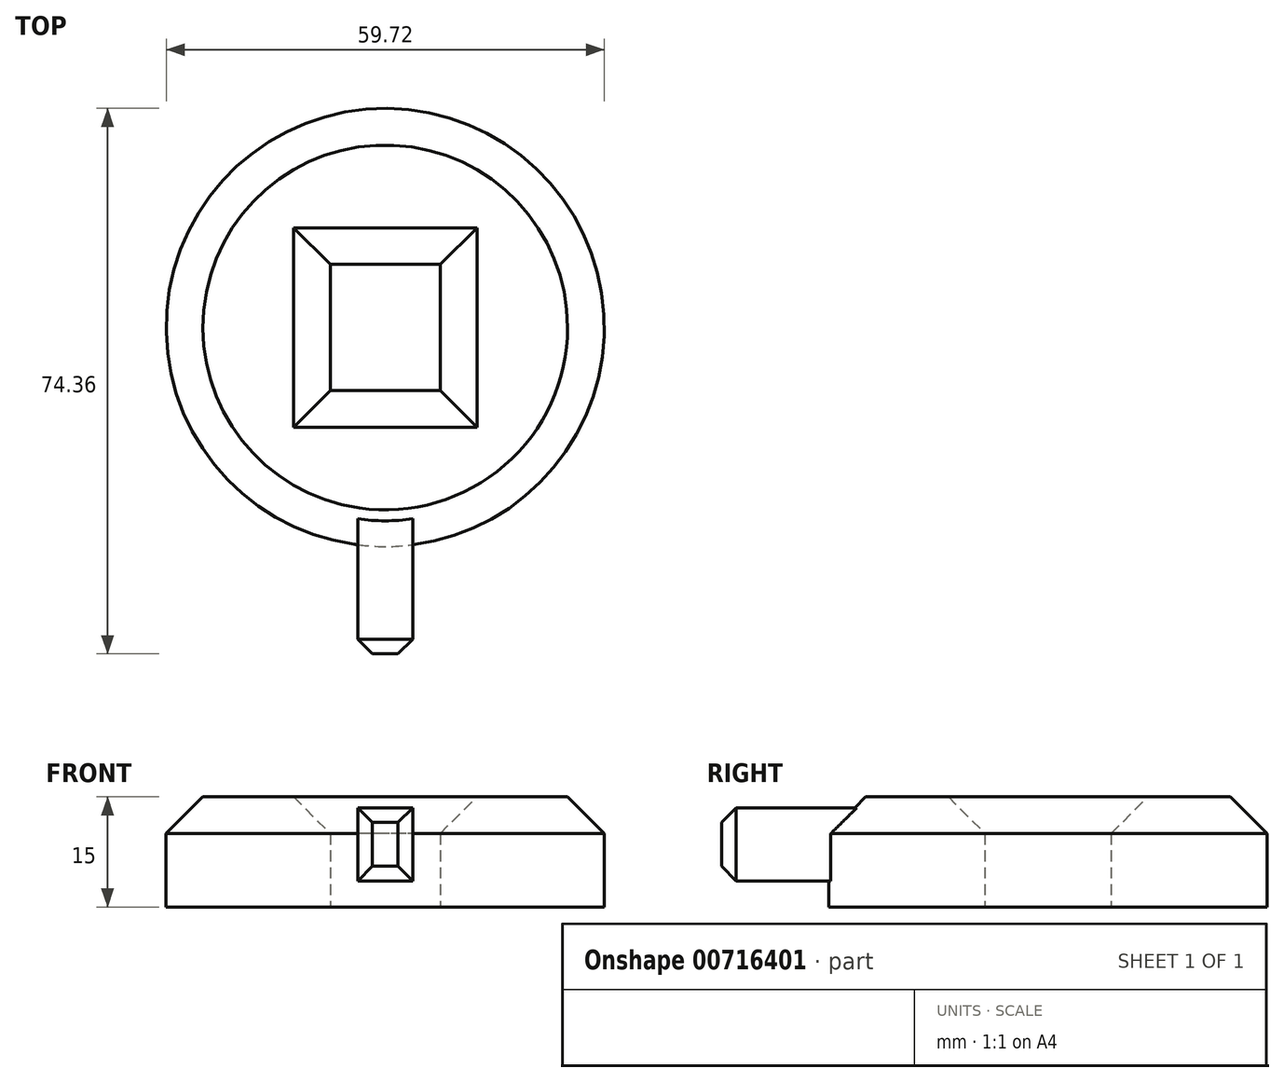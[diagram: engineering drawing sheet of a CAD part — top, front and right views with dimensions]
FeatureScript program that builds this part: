
annotation { "Feature Type Name" : "Feature", "Feature Type Description" : "" }
export const myFeature = defineFeature(function(context is Context, id is Id, definition is map)
    precondition{}
    {
        {
            var Q0;
            Q0=qCreatedBy(makeId("Top.planeOp"),FACE);
            var sketch = newSketch(context, id + "F0", { "sketchPlane" : qUnion([Q0])});
            skCircle(sketch, "E0", {"center": v(0, 0) * mm, "radius": 29.86 * mm});
            skLineSegment(sketch, "E1.bottom", {"start": v(-7.5, 8.59) * mm, "end": v(7.5, 8.59) * mm});
            skLineSegment(sketch, "E1.top", {"start": v(-7.5, -8.59) * mm, "end": v(7.5, -8.59) * mm});
            skLineSegment(sketch, "E1.left", {"start": v(-7.5, 8.59) * mm, "end": v(-7.5, -8.59) * mm});
            skLineSegment(sketch, "E1.right", {"start": v(7.5, 8.59) * mm, "end": v(7.5, -8.59) * mm});
            skSolve(sketch);
        }
        {
            var Q0;
            Q0=makeQuery(id+"F0.imprint","IMPRINT",FACE,{"disambiguationData":[TD([[makeQuery(id+"F0.imprint","IMPRINT",EDGE,{"derivedFrom":sQuery(id+"F0.wireOp",EDGE,"E0")}),1.0]])]});
            extrude(context, id + "F1", {"entities" : qUnion([Q0]), "depth" : 15 * mm, "offsetDistance" : 25 * mm});
        }
        {
            var Q0;
            Q0=qCreatedBy(makeId("Front.planeOp"),FACE);
            cPlane(context, id + "F2", {"entities" : qUnion([Q0]), "cplaneType" : CPlaneType.OFFSET, "offset" : 24.5 * mm, "width" : 150 * mm, "height" : 150 * mm});
        }
        {
            var Q0;
            Q0=qCreatedBy(id+"F2.planeOp",FACE);
            var sketch = newSketch(context, id + "F3", { "sketchPlane" : qUnion([Q0])});
            skLineSegment(sketch, "E2.bottom", {"start": v(3.74, 3.54) * mm, "end": v(-3.74, 3.54) * mm});
            skLineSegment(sketch, "E2.top", {"start": v(3.74, 13.5) * mm, "end": v(-3.74, 13.5) * mm});
            skLineSegment(sketch, "E2.left", {"start": v(3.74, 3.54) * mm, "end": v(3.74, 13.5) * mm});
            skLineSegment(sketch, "E2.right", {"start": v(-3.74, 3.54) * mm, "end": v(-3.74, 13.5) * mm});
            skPoint(sketch, "E2.middle", {"position": v(0, 8.53) * mm});
            skSolve(sketch);
        }
        {
            var Q0;
            Q0 = qSketchRegion(id + "F3", true);
            extrude(context, id + "F4", {"entities" : qUnion([Q0]), "operationType" : NewBodyOperationType.ADD, "depth" : 20 * mm, "offsetDistance" : 25 * mm});
        }
        {
            var Q0;
            Q0=makeQuery(id+"F4.opExtrude","CAP_FACE",FACE,{"disambiguationData":[OSD([sQuery(id+"F3.wireOp",EDGE,"E2.bottom"),sQuery(id+"F3.wireOp",EDGE,"E2.top"),sQuery(id+"F3.wireOp",EDGE,"E2.left"),sQuery(id+"F3.wireOp",EDGE,"E2.right")])],"isStart":false});
            chamfer(context, id + "F5", {"entities" : qUnion([Q0]), "width" : 2 * mm, "tangentPropagation" : true});
        }
        {
            var Q0;
            Q0=makeQuery(id+"F1.opExtrude","CAP_FACE",FACE,{"disambiguationData":[OSD([sQuery(id+"F0.wireOp",EDGE,"E0"),sQuery(id+"F0.wireOp",EDGE,"E1.bottom"),sQuery(id+"F0.wireOp",EDGE,"E1.top"),sQuery(id+"F0.wireOp",EDGE,"E1.left"),sQuery(id+"F0.wireOp",EDGE,"E1.right")])],"isStart":false});
            chamfer(context, id + "F6", {"entities" : qUnion([Q0]), "width" : 5 * mm, "tangentPropagation" : true});
        }
    });
